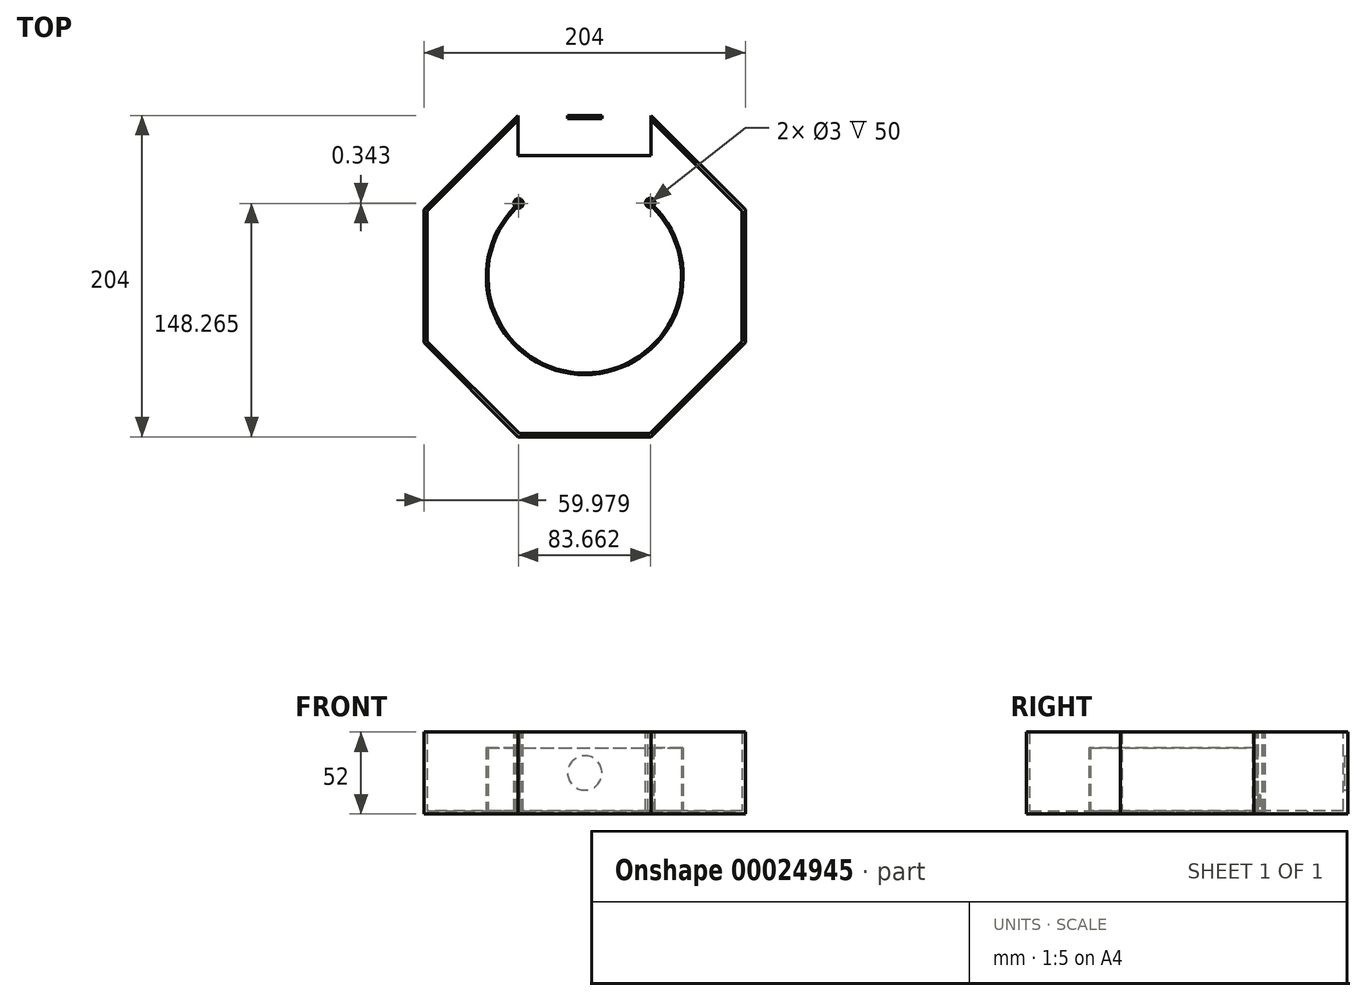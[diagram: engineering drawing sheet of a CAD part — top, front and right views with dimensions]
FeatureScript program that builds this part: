
annotation { "Feature Type Name" : "Feature", "Feature Type Description" : "" }
export const myFeature = defineFeature(function(context is Context, id is Id, definition is map)
    precondition{}
    {
        {
            var Q0;
            Q0=qCreatedBy(makeId("Top.planeOp"),FACE);
            var sketch = newSketch(context, id + "F0", { "sketchPlane" : qUnion([Q0])});
            skCircle(sketch, "E0.cCircle", {"center": v(0, 0) * mm, "radius": 102 * mm, "construction": true});
            skLineSegment(sketch, "E0.0", {"start": v(42.25, -102) * mm, "end": v(-42.25, -102) * mm});
            skLineSegment(sketch, "E0.1", {"start": v(-42.25, -102) * mm, "end": v(-102, -42.25) * mm});
            skLineSegment(sketch, "E0.2", {"start": v(-102, -42.25) * mm, "end": v(-102, 42.25) * mm});
            skLineSegment(sketch, "E0.3", {"start": v(-102, 42.25) * mm, "end": v(-42.25, 102) * mm});
            skLineSegment(sketch, "E0.4", {"start": v(-42.25, 102) * mm, "end": v(42.25, 102) * mm});
            skLineSegment(sketch, "E0.5", {"start": v(42.25, 102) * mm, "end": v(102, 42.25) * mm});
            skLineSegment(sketch, "E0.6", {"start": v(102, 42.25) * mm, "end": v(102, -42.25) * mm});
            skLineSegment(sketch, "E0.7", {"start": v(102, -42.25) * mm, "end": v(42.25, -102) * mm});
            skPoint(sketch, "E0.0.midPoint", {"position": v(0, -102) * mm});
            skCircle(sketch, "E1.cCircle", {"center": v(0, 0) * mm, "radius": 100 * mm, "construction": true});
            skLineSegment(sketch, "E1.0", {"start": v(41.42, -100) * mm, "end": v(-41.42, -100) * mm});
            skLineSegment(sketch, "E1.1", {"start": v(-41.42, -100) * mm, "end": v(-100, -41.42) * mm});
            skLineSegment(sketch, "E1.2", {"start": v(-100, -41.42) * mm, "end": v(-100, 41.42) * mm});
            skLineSegment(sketch, "E1.3", {"start": v(-100, 41.42) * mm, "end": v(-41.42, 100) * mm});
            skLineSegment(sketch, "E1.4", {"start": v(-41.42, 100) * mm, "end": v(41.42, 100) * mm});
            skLineSegment(sketch, "E1.5", {"start": v(41.42, 100) * mm, "end": v(100, 41.42) * mm});
            skLineSegment(sketch, "E1.6", {"start": v(100, 41.42) * mm, "end": v(100, -41.42) * mm});
            skLineSegment(sketch, "E1.7", {"start": v(100, -41.42) * mm, "end": v(41.42, -100) * mm});
            skPoint(sketch, "E1.0.midPoint", {"position": v(0, -100) * mm});
            skCircle(sketch, "E2", {"center": v(0, 0) * mm, "radius": 61.5 * mm});
            skCircle(sketch, "E3", {"center": v(0, 0) * mm, "radius": 62.5 * mm});
            skLineSegment(sketch, "E4", {"start": v(-42.25, 102) * mm, "end": v(-41.42, -100) * mm});
            skLineSegment(sketch, "E5", {"start": v(41.42, 100) * mm, "end": v(42.25, -102) * mm});
            skSolve(sketch);
        }
        {
            var Q0;
            Q0 = qSketchRegion(id + "F0", true);
            var Q1;
            {var subQ3=sQuery(id+"F0.wireOp",EDGE,"E1.1");Q1=makeQuery(id+"F0.imprint","IMPRINT",FACE,{"disambiguationData":[TD([[makeQuery(id+"F0.imprint","IMPRINT",EDGE,{"derivedFrom":subQ3}),-1.0]])]});}
            var Q2;
            {var subQ7=sQuery(id+"F0.wireOp",EDGE,"E1.0");Q2=makeQuery(id+"F0.imprint","IMPRINT",FACE,{"disambiguationData":[TD([[makeQuery(id+"F0.imprint","IMPRINT",EDGE,{"derivedFrom":subQ7}),-1.0]])]});}
            var Q3;
            {var subQ6=sQuery(id+"F0.wireOp",EDGE,"E1.5");Q3=makeQuery(id+"F0.imprint","IMPRINT",FACE,{"disambiguationData":[TD([[makeQuery(id+"F0.imprint","IMPRINT",EDGE,{"derivedFrom":subQ6}),-1.0]])]});}
            var Q4;
            {var subQ0=sQuery(id+"F0.wireOp",EDGE,"E4");var subQ1=sQuery(id+"F0.wireOp",EDGE,"E2");var subQ3=makeQuery(id+"F0.imprint","INTERSECT",VERTEX,{"disambiguationData":[OD(0.0)],"derivedFrom":[subQ1,subQ0]});Q4=makeQuery(id+"F0.imprint","IMPRINT",FACE,{"disambiguationData":[TD([[makeQuery(id+"F0.imprint","IMPRINT",EDGE,{"disambiguationData":[TD([[subQ3,1.0]])],"derivedFrom":subQ1}),1.0]])]});}
            var Q5;
            {var subQ3=sQuery(id+"F0.wireOp",EDGE,"E1.4");Q5=makeQuery(id+"F0.imprint","IMPRINT",FACE,{"disambiguationData":[TD([[makeQuery(id+"F0.imprint","IMPRINT",EDGE,{"derivedFrom":subQ3}),-1.0]])]});}
            var Q6;
            {var subQ0=sQuery(id+"F0.wireOp",EDGE,"E5");var subQ1=sQuery(id+"F0.wireOp",EDGE,"E2");var subQ3=makeQuery(id+"F0.imprint","INTERSECT",VERTEX,{"disambiguationData":[OD(0.0)],"derivedFrom":[subQ1,subQ0]});Q6=makeQuery(id+"F0.imprint","IMPRINT",FACE,{"disambiguationData":[TD([[makeQuery(id+"F0.imprint","IMPRINT",EDGE,{"disambiguationData":[TD([[subQ3,1.0]])],"derivedFrom":subQ1}),1.0]])]});}
            var Q7;
            {var subQ0=sQuery(id+"F0.wireOp",EDGE,"E4");var subQ1=sQuery(id+"F0.wireOp",EDGE,"E2");var subQ3=makeQuery(id+"F0.imprint","INTERSECT",VERTEX,{"disambiguationData":[OD(0.0)],"derivedFrom":[subQ1,subQ0]});Q7=makeQuery(id+"F0.imprint","IMPRINT",FACE,{"disambiguationData":[TD([[makeQuery(id+"F0.imprint","IMPRINT",EDGE,{"disambiguationData":[TD([[subQ3,-1.0]])],"derivedFrom":subQ1}),1.0]])]});}
            var Q8;
            {var subQ3=sQuery(id+"F0.wireOp",EDGE,"E2");var subQ5=sQuery(id+"F0.wireOp",EDGE,"E4");var subQ7=makeQuery(id+"F0.imprint","INTERSECT",VERTEX,{"disambiguationData":[OD(1.0)],"derivedFrom":[subQ3,subQ5]});Q8=makeQuery(id+"F0.imprint","IMPRINT",FACE,{"disambiguationData":[TD([[makeQuery(id+"F0.imprint","IMPRINT",EDGE,{"disambiguationData":[TD([[subQ7,-1.0]])],"derivedFrom":subQ3}),-1.0]])]});}
            var Q9;
            {var subQ0=sQuery(id+"F0.wireOp",EDGE,"E5");var subQ3=sQuery(id+"F0.wireOp",EDGE,"E2");var subQ6=makeQuery(id+"F0.imprint","INTERSECT",VERTEX,{"disambiguationData":[OD(0.0)],"derivedFrom":[subQ3,subQ0]});Q9=makeQuery(id+"F0.imprint","IMPRINT",FACE,{"disambiguationData":[TD([[makeQuery(id+"F0.imprint","IMPRINT",EDGE,{"disambiguationData":[TD([[subQ6,1.0]])],"derivedFrom":subQ3}),-1.0]])]});}
            var Q10;
            {var subQ3=sQuery(id+"F0.wireOp",EDGE,"E2");var subQ5=sQuery(id+"F0.wireOp",EDGE,"E4");var subQ7=makeQuery(id+"F0.imprint","INTERSECT",VERTEX,{"disambiguationData":[OD(0.0)],"derivedFrom":[subQ3,subQ5]});Q10=makeQuery(id+"F0.imprint","IMPRINT",FACE,{"disambiguationData":[TD([[makeQuery(id+"F0.imprint","IMPRINT",EDGE,{"disambiguationData":[TD([[subQ7,1.0]])],"derivedFrom":subQ3}),-1.0]])]});}
            var Q11;
            {var subQ0=sQuery(id+"F0.wireOp",EDGE,"E4");var subQ3=sQuery(id+"F0.wireOp",EDGE,"E2");var subQ6=makeQuery(id+"F0.imprint","INTERSECT",VERTEX,{"disambiguationData":[OD(0.0)],"derivedFrom":[subQ3,subQ0]});Q11=makeQuery(id+"F0.imprint","IMPRINT",FACE,{"disambiguationData":[TD([[makeQuery(id+"F0.imprint","IMPRINT",EDGE,{"disambiguationData":[TD([[subQ6,-1.0]])],"derivedFrom":subQ3}),-1.0]])]});}
            extrude(context, id + "F1", {"entities" : qUnion([Q0, Q1, Q2, Q3, Q4, Q5, Q6, Q7, Q8, Q9, Q10, Q11]), "oppositeDirection" : true, "depth" : 2 * mm});
        }
        {
            var Q0;
            Q0 = qSketchRegion(id + "F0", true);
            extrude(context, id + "F2", {"entities" : qUnion([Q0]), "operationType" : NewBodyOperationType.ADD, "depth" : 50 * mm});
        }
        {
            var Q0;
            {var subQ0=sQuery(id+"F0.wireOp",EDGE,"E4");var subQ3=sQuery(id+"F0.wireOp",EDGE,"E2");var subQ6=makeQuery(id+"F0.imprint","INTERSECT",VERTEX,{"disambiguationData":[OD(0.0)],"derivedFrom":[subQ3,subQ0]});Q0=makeQuery(id+"F0.imprint","IMPRINT",FACE,{"disambiguationData":[TD([[makeQuery(id+"F0.imprint","IMPRINT",EDGE,{"disambiguationData":[TD([[subQ6,-1.0]])],"derivedFrom":subQ3}),-1.0]])]});}
            var Q1;
            {var subQ3=sQuery(id+"F0.wireOp",EDGE,"E2");var subQ5=sQuery(id+"F0.wireOp",EDGE,"E4");var subQ7=makeQuery(id+"F0.imprint","INTERSECT",VERTEX,{"disambiguationData":[OD(1.0)],"derivedFrom":[subQ3,subQ5]});Q1=makeQuery(id+"F0.imprint","IMPRINT",FACE,{"disambiguationData":[TD([[makeQuery(id+"F0.imprint","IMPRINT",EDGE,{"disambiguationData":[TD([[subQ7,-1.0]])],"derivedFrom":subQ3}),-1.0]])]});}
            var Q2;
            {var subQ0=sQuery(id+"F0.wireOp",EDGE,"E5");var subQ3=sQuery(id+"F0.wireOp",EDGE,"E2");var subQ6=makeQuery(id+"F0.imprint","INTERSECT",VERTEX,{"disambiguationData":[OD(0.0)],"derivedFrom":[subQ3,subQ0]});Q2=makeQuery(id+"F0.imprint","IMPRINT",FACE,{"disambiguationData":[TD([[makeQuery(id+"F0.imprint","IMPRINT",EDGE,{"disambiguationData":[TD([[subQ6,1.0]])],"derivedFrom":subQ3}),-1.0]])]});}
            extrude(context, id + "F3", {"entities" : qUnion([Q0, Q1, Q2]), "operationType" : NewBodyOperationType.ADD, "depth" : 40 * mm});
        }
        {
            var Q0;
            {var subQ0=sQuery(id+"F0.wireOp",EDGE,"E0.4");Q0=makeQuery(id+"F2.boolean.opBoolean","MERGE",FACE,{"derivedFrom":[makeQuery(id+"F1.opExtrude","SWEPT_FACE",FACE,{"disambiguationData":[OSD([subQ0])]}),makeQuery(id+"F2.opExtrude","SWEPT_FACE",FACE,{"disambiguationData":[OSD([subQ0])]})]});}
            var sketch = newSketch(context, id + "F4", { "sketchPlane" : qUnion([Q0])});
            skLineSegment(sketch, "E6", {"start": v(42.25, 24) * mm, "end": v(-42.25, 24) * mm});
            skCircle(sketch, "E7", {"center": v(0, 24) * mm, "radius": 10.9 * mm});
            skSolve(sketch);
        }
        {
            var Q0;
            {var subQ0=sQuery(id+"F4.wireOp",EDGE,"E7");var subQ1=sQuery(id+"F4.wireOp",EDGE,"E6");var subQ3=makeQuery(id+"F4.imprint","INTERSECT",VERTEX,{"disambiguationData":[OD(0.0)],"derivedFrom":[subQ1,subQ0]});Q0=makeQuery(id+"F4.imprint","IMPRINT",FACE,{"disambiguationData":[TD([[makeQuery(id+"F4.imprint","IMPRINT",EDGE,{"disambiguationData":[TD([[subQ3,-1.0]])],"derivedFrom":subQ1}),-1.0]])]});}
            var Q1;
            {var subQ0=sQuery(id+"F4.wireOp",EDGE,"E7");var subQ1=sQuery(id+"F4.wireOp",EDGE,"E6");var subQ3=makeQuery(id+"F4.imprint","INTERSECT",VERTEX,{"disambiguationData":[OD(0.0)],"derivedFrom":[subQ1,subQ0]});Q1=makeQuery(id+"F4.imprint","IMPRINT",FACE,{"disambiguationData":[TD([[makeQuery(id+"F4.imprint","IMPRINT",EDGE,{"disambiguationData":[TD([[subQ3,-1.0]])],"derivedFrom":subQ1}),1.0]])]});}
            extrude(context, id + "F5", {"entities" : qUnion([Q0, Q1]), "operationType" : NewBodyOperationType.REMOVE, "oppositeDirection" : true, "depth" : 25.4 * mm});
        }
        {
            var Q0;
            Q0=makeQuery(id+"F3.opExtrude","CAP_FACE",FACE,{"disambiguationData":[OSD([sQuery(id+"F0.wireOp",EDGE,"E2"),sQuery(id+"F0.wireOp",EDGE,"E3"),sQuery(id+"F0.wireOp",EDGE,"E4"),sQuery(id+"F0.wireOp",EDGE,"E5")])],"isStart":false});
            var sketch = newSketch(context, id + "F6", { "sketchPlane" : qUnion([Q0])});
            skCircle(sketch, "E8", {"center": v(-42.02, 46.27) * mm, "radius": 3 * mm});
            skCircle(sketch, "E9", {"center": v(-42.02, 46.27) * mm, "radius": 1.5 * mm});
            skSolve(sketch);
        }
        {
            var Q0;
            Q0 = qSketchRegion(id + "F6", true);
            extrude(context, id + "F7", {"entities" : qUnion([Q0]), "operationType" : NewBodyOperationType.ADD, "oppositeDirection" : true, "depth" : 40 * mm, "hasSecondDirection" : true, "secondDirectionOppositeDirection" : false, "secondDirectionDepth" : 10 * mm});
        }
        {
            var Q0;
            Q0=makeQuery(id+"F7.boolean.opBoolean","MERGE",FACE,{"derivedFrom":[makeQuery(id+"F3.opExtrude","CAP_FACE",FACE,{"disambiguationData":[OSD([sQuery(id+"F0.wireOp",EDGE,"E2"),sQuery(id+"F0.wireOp",EDGE,"E3"),sQuery(id+"F0.wireOp",EDGE,"E4"),sQuery(id+"F0.wireOp",EDGE,"E5")])],"isStart":false}),makeQuery(id+"F7.opExtrude","CAP_FACE",FACE,{"disambiguationData":[OSD([sQuery(id+"F6.wireOp",EDGE,"E8"),sQuery(id+"F6.wireOp",EDGE,"E9")])],"isStart":true})]});
            var sketch = newSketch(context, id + "F8", { "sketchPlane" : qUnion([Q0])});
            skCircle(sketch, "E10", {"center": v(-42.02, 46.27) * mm, "radius": 1.5 * mm});
            skSolve(sketch);
        }
        {
            var Q0;
            Q0 = qSketchRegion(id + "F8", true);
            extrude(context, id + "F9", {"entities" : qUnion([Q0]), "operationType" : NewBodyOperationType.REMOVE, "oppositeDirection" : true, "depth" : 40 * mm});
        }
        {
            var Q0;
            Q0=makeQuery(id+"F7.boolean.opBoolean","MERGE",FACE,{"derivedFrom":[makeQuery(id+"F3.opExtrude","CAP_FACE",FACE,{"disambiguationData":[OSD([sQuery(id+"F0.wireOp",EDGE,"E2"),sQuery(id+"F0.wireOp",EDGE,"E3"),sQuery(id+"F0.wireOp",EDGE,"E4"),sQuery(id+"F0.wireOp",EDGE,"E5")])],"isStart":false}),makeQuery(id+"F7.opExtrude","CAP_FACE",FACE,{"disambiguationData":[OSD([sQuery(id+"F6.wireOp",EDGE,"E8"),sQuery(id+"F6.wireOp",EDGE,"E9")])],"isStart":true})]});
            var sketch = newSketch(context, id + "F10", { "sketchPlane" : qUnion([Q0])});
            skCircle(sketch, "E11", {"center": v(41.64, 46.6) * mm, "radius": 3 * mm});
            skCircle(sketch, "E12", {"center": v(41.64, 46.6) * mm, "radius": 1.5 * mm});
            skSolve(sketch);
        }
        {
            var Q0;
            Q0 = qSketchRegion(id + "F10", true);
            extrude(context, id + "F11", {"entities" : qUnion([Q0]), "operationType" : NewBodyOperationType.ADD, "endBound" : BoundingType.UP_TO_NEXT, "oppositeDirection" : true, "depth" : 50 * mm});
        }
        {
            var Q0;
            Q0=makeQuery(id+"F11.boolean.opBoolean","MERGE",FACE,{"derivedFrom":[makeQuery(id+"F7.boolean.opBoolean","MERGE",FACE,{"derivedFrom":[makeQuery(id+"F3.opExtrude","CAP_FACE",FACE,{"disambiguationData":[OSD([sQuery(id+"F0.wireOp",EDGE,"E2"),sQuery(id+"F0.wireOp",EDGE,"E3"),sQuery(id+"F0.wireOp",EDGE,"E4"),sQuery(id+"F0.wireOp",EDGE,"E5")])],"isStart":false}),makeQuery(id+"F7.opExtrude","CAP_FACE",FACE,{"disambiguationData":[OSD([sQuery(id+"F6.wireOp",EDGE,"E8"),sQuery(id+"F6.wireOp",EDGE,"E9")])],"isStart":true})]}),makeQuery(id+"F11.opExtrude","CAP_FACE",FACE,{"disambiguationData":[OSD([sQuery(id+"F10.wireOp",EDGE,"E11"),sQuery(id+"F10.wireOp",EDGE,"E12")])],"isStart":true})]});
            var sketch = newSketch(context, id + "F12", { "sketchPlane" : qUnion([Q0])});
            skCircle(sketch, "E13", {"center": v(41.64, 46.6) * mm, "radius": 1.5 * mm});
            skSolve(sketch);
        }
        {
            var Q0;
            Q0 = qSketchRegion(id + "F12", true);
            extrude(context, id + "F13", {"entities" : qUnion([Q0]), "operationType" : NewBodyOperationType.REMOVE, "oppositeDirection" : true, "depth" : 40 * mm});
        }
    });
